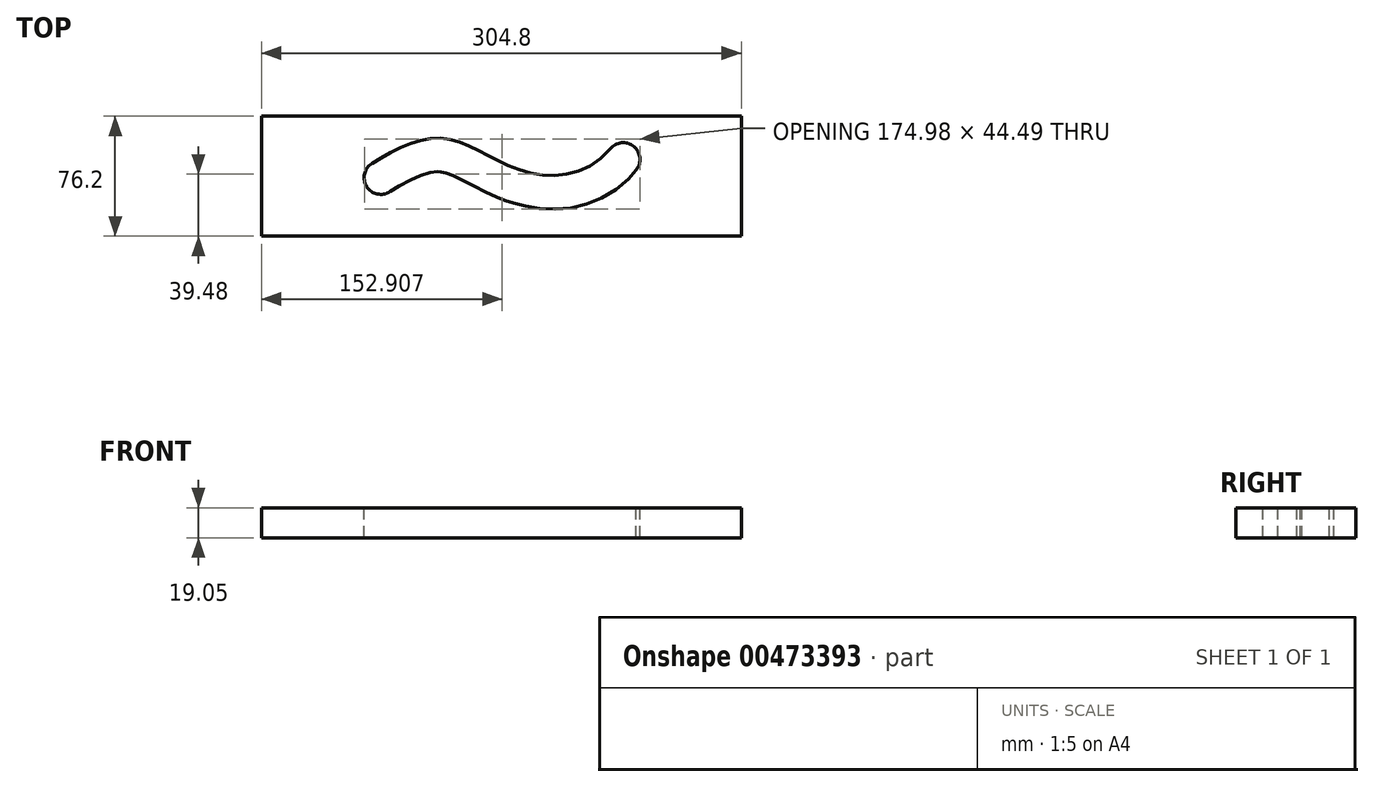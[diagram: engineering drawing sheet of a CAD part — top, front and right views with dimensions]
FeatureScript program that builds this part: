
annotation { "Feature Type Name" : "Feature", "Feature Type Description" : "" }
export const myFeature = defineFeature(function(context is Context, id is Id, definition is map)
    precondition{}
    {
        {
            var Q0;
            Q0=qCreatedBy(makeId("Top.planeOp"),FACE);
            var sketch = newSketch(context, id + "F0", { "sketchPlane" : qUnion([Q0])});
            skLineSegment(sketch, "E0.bottom", {"start": v(0, 0) * mm, "end": v(304.8, 0) * mm});
            skLineSegment(sketch, "E0.top", {"start": v(0, -76.2) * mm, "end": v(304.8, -76.2) * mm});
            skLineSegment(sketch, "E0.left", {"start": v(0, 0) * mm, "end": v(0, -76.2) * mm});
            skLineSegment(sketch, "E0.right", {"start": v(304.8, 0) * mm, "end": v(304.8, -76.2) * mm});
            skSolve(sketch);
        }
        {
            var Q0;
            Q0=makeQuery(id+"F0.imprint","IMPRINT",FACE,{"disambiguationData":[TD([[makeQuery(id+"F0.imprint","IMPRINT",EDGE,{"derivedFrom":sQuery(id+"F0.wireOp",EDGE,"E0.bottom")}),-1.0]])]});
            extrude(context, id + "F1", {"entities" : qUnion([Q0]), "depth" : 19.05 * mm});
        }
        {
            var Q0;
            Q0=makeQuery(id+"F1.opExtrude","CAP_FACE",FACE,{"disambiguationData":[OSD([sQuery(id+"F0.wireOp",EDGE,"E0.bottom"),sQuery(id+"F0.wireOp",EDGE,"E0.top"),sQuery(id+"F0.wireOp",EDGE,"E0.left"),sQuery(id+"F0.wireOp",EDGE,"E0.right")])],"isStart":false});
            var sketch = newSketch(context, id + "F2", { "sketchPlane" : qUnion([Q0])});
            skFitSpline(sketch, "E1", {"points": [v(70.16, -30.03) * mm, v(115.84, -14.1) * mm, v(162.33, -33.54) * mm, v(221.51, -20.73) * mm], "startDerivative": vector(129.13, 82.78) * mm, "endDerivative": vector(133.8, 164.46) * mm});
            skFitSpline(sketch, "E2.0", {"points": [v(81.67, -48) * mm, v(84.09, -46.44) * mm, v(87.8, -44.18) * mm, v(92.75, -41.5) * mm, v(96.4, -39.71) * mm, v(99.95, -38.19) * mm, v(103.32, -36.96) * mm, v(106.44, -36.06) * mm, v(108.77, -35.6) * mm, v(110.43, -35.38) * mm, v(111.58, -35.3) * mm, v(112.44, -35.27) * mm, v(113.07, -35.29) * mm, v(113.45, -35.3) * mm, v(113.74, -35.33) * mm, v(114.01, -35.36) * mm, v(114.37, -35.4) * mm, v(114.82, -35.47) * mm, v(115.46, -35.58) * mm, v(116.32, -35.77) * mm, v(117.47, -36.1) * mm, v(118.74, -36.51) * mm, v(120.6, -37.2) * mm, v(123.21, -38.35) * mm, v(126.81, -40.12) * mm, v(130.84, -42.23) * mm, v(135.3, -44.62) * mm, v(140.2, -47.17) * mm, v(144.66, -49.34) * mm, v(148.48, -51.03) * mm, v(151.48, -52.27) * mm, v(154.09, -53.26) * mm, v(156.24, -54.01) * mm, v(158.42, -54.73) * mm, v(161.2, -55.57) * mm, v(165.73, -56.76) * mm, v(171.57, -57.95) * mm, v(178.86, -58.82) * mm, v(186.37, -59.06) * mm, v(194.08, -58.55) * mm, v(201.91, -57.18) * mm, v(209.77, -54.83) * mm, v(217.5, -51.4) * mm, v(224.93, -46.85) * mm, v(231.88, -41.15) * mm, v(236.09, -36.63) * mm, v(238.06, -34.2) * mm]});
            skArc(sketch, "E3", {"start": v(70.16, -30.03) * mm, "mid": v(66.93, -44.77) * mm, "end": v(81.67, -48) * mm});
            skArc(sketch, "E4", {"start": v(238.06, -34.2) * mm, "mid": v(236.52, -19.2) * mm, "end": v(221.51, -20.73) * mm});
            skSolve(sketch);
        }
        {
            var Q0;
            Q0=makeQuery(id+"F2.imprint","IMPRINT",FACE,{"disambiguationData":[TD([[makeQuery(id+"F2.imprint","IMPRINT",EDGE,{"derivedFrom":sQuery(id+"F2.wireOp",EDGE,"E1")}),-1.0]])]});
            extrude(context, id + "F3", {"entities" : qUnion([Q0]), "operationType" : NewBodyOperationType.REMOVE, "endBound" : BoundingType.THROUGH_ALL, "oppositeDirection" : true, "depth" : 25.4 * mm});
        }
    });
